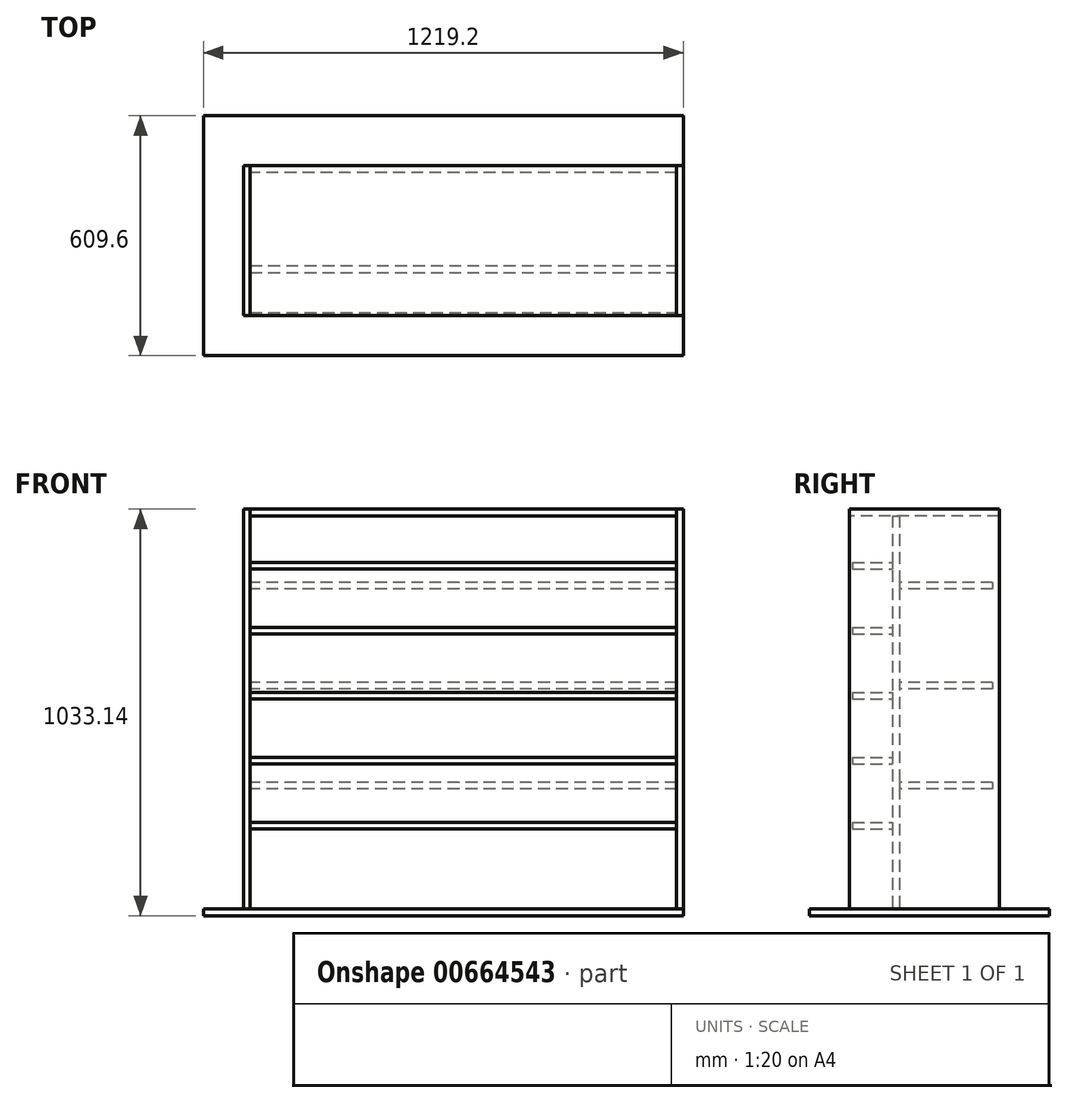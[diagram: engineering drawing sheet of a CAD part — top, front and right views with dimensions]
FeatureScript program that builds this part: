
annotation { "Feature Type Name" : "Feature", "Feature Type Description" : "" }
export const myFeature = defineFeature(function(context is Context, id is Id, definition is map)
    precondition{}
    {
        {
            var Q0;
            Q0=qCreatedBy(makeId("Top.planeOp"),FACE);
            var sketch = newSketch(context, id + "F0", { "sketchPlane" : qUnion([Q0])});
            skLineSegment(sketch, "E0.bottom", {"start": v(0, 0) * mm, "end": v(1219.2, 0) * mm});
            skLineSegment(sketch, "E0.top", {"start": v(0, 609.6) * mm, "end": v(1219.2, 609.6) * mm});
            skLineSegment(sketch, "E0.left", {"start": v(0, 0) * mm, "end": v(0, 609.6) * mm});
            skLineSegment(sketch, "E0.right", {"start": v(1219.2, 0) * mm, "end": v(1219.2, 609.6) * mm});
            skSolve(sketch);
        }
        {
            var Q0;
            Q0 = qSketchRegion(id + "F0", true);
            extrude(context, id + "F1", {"entities" : qUnion([Q0]), "depth" : 17.14 * mm, "offsetDistance" : 25.4 * mm});
        }
        {
            var Q0;
            Q0=makeQuery(id+"F1.opExtrude","CAP_FACE",FACE,{"disambiguationData":[OSD([sQuery(id+"F0.wireOp",EDGE,"E0.bottom"),sQuery(id+"F0.wireOp",EDGE,"E0.top"),sQuery(id+"F0.wireOp",EDGE,"E0.left"),sQuery(id+"F0.wireOp",EDGE,"E0.right")])],"isStart":false});
            var sketch = newSketch(context, id + "F2", { "sketchPlane" : qUnion([Q0])});
            skLineSegment(sketch, "E1.bottom", {"start": v(118.75, 101.6) * mm, "end": v(101.6, 101.6) * mm});
            skLineSegment(sketch, "E1.top", {"start": v(118.74, 482.6) * mm, "end": v(101.6, 482.6) * mm});
            skLineSegment(sketch, "E1.left", {"start": v(118.75, 101.6) * mm, "end": v(118.74, 482.6) * mm});
            skLineSegment(sketch, "E1.right", {"start": v(101.6, 101.6) * mm, "end": v(101.6, 482.6) * mm});
            skSolve(sketch);
        }
        {
            var Q0;
            Q0=makeQuery(id+"F2.imprint","IMPRINT",FACE,{"disambiguationData":[TD([[makeQuery(id+"F2.imprint","IMPRINT",EDGE,{"derivedFrom":sQuery(id+"F2.wireOp",EDGE,"E1.bottom")}),-1.0]])]});
            extrude(context, id + "F3", {"entities" : qUnion([Q0]), "depth" : 1016 * mm, "offsetDistance" : 25.4 * mm});
        }
        {
            var Q0;
            {var subQ0=sQuery(id+"F0.wireOp",EDGE,"E0.top");var subQ1=sQuery(id+"F0.wireOp",EDGE,"E0.right");var subQ2=sQuery(id+"F0.wireOp",EDGE,"E0.bottom");Q0=makeQuery(id+"F3.boolean.opBoolean","SPLIT",FACE,{"disambiguationData":[TD([makeQuery(id+"F1.opExtrude","SWEPT_FACE",FACE,{"disambiguationData":[OSD([subQ1])]})])],"derivedFrom":makeQuery(id+"F1.opExtrude","CAP_FACE",FACE,{"disambiguationData":[OSD([subQ2,subQ0,sQuery(id+"F0.wireOp",EDGE,"E0.left"),subQ1])],"isStart":false})});}
            var sketch = newSketch(context, id + "F4", { "sketchPlane" : qUnion([Q0])});
            skLineSegment(sketch, "E2.bottom", {"start": v(118.74, 211.45) * mm, "end": v(1202.06, 211.45) * mm});
            skLineSegment(sketch, "E2.top", {"start": v(118.74, 228.6) * mm, "end": v(1202.06, 228.6) * mm});
            skLineSegment(sketch, "E2.left", {"start": v(118.75, 211.45) * mm, "end": v(118.75, 228.6) * mm});
            skLineSegment(sketch, "E2.right", {"start": v(1202.06, 211.46) * mm, "end": v(1202.06, 228.6) * mm});
            skSolve(sketch);
        }
        {
            var Q0;
            Q0 = qSketchRegion(id + "F4", true);
            extrude(context, id + "F5", {"entities" : qUnion([Q0]), "depth" : 998.86 * mm, "offsetDistance" : 25.4 * mm});
        }
        {
            var Q0;
            {var subQ0=sQuery(id+"F0.wireOp",EDGE,"E0.top");var subQ1=sQuery(id+"F0.wireOp",EDGE,"E0.right");var subQ2=sQuery(id+"F0.wireOp",EDGE,"E0.bottom");Q0=makeQuery(id+"F3.boolean.opBoolean","SPLIT",FACE,{"disambiguationData":[TD([makeQuery(id+"F1.opExtrude","SWEPT_FACE",FACE,{"disambiguationData":[OSD([subQ1])]})])],"derivedFrom":makeQuery(id+"F1.opExtrude","CAP_FACE",FACE,{"disambiguationData":[OSD([subQ2,subQ0,sQuery(id+"F0.wireOp",EDGE,"E0.left"),subQ1])],"isStart":false})});}
            var sketch = newSketch(context, id + "F6", { "sketchPlane" : qUnion([Q0])});
            skLineSegment(sketch, "E3.bottom", {"start": v(1219.2, 101.6) * mm, "end": v(1202.06, 101.6) * mm});
            skLineSegment(sketch, "E3.top", {"start": v(1219.2, 482.6) * mm, "end": v(1202.06, 482.6) * mm});
            skLineSegment(sketch, "E3.left", {"start": v(1219.2, 101.6) * mm, "end": v(1219.2, 482.6) * mm});
            skLineSegment(sketch, "E3.right", {"start": v(1202.06, 101.6) * mm, "end": v(1202.06, 482.6) * mm});
            skSolve(sketch);
        }
        {
            var Q0;
            Q0 = qSketchRegion(id + "F6", true);
            extrude(context, id + "F7", {"entities" : qUnion([Q0]), "depth" : 1016 * mm, "offsetDistance" : 25.4 * mm});
        }
        {
            var Q0;
            Q0=makeQuery(id+"F5.opExtrude","SWEPT_FACE",FACE,{"disambiguationData":[OSD([sQuery(id+"F4.wireOp",EDGE,"E2.top")])]});
            var sketch = newSketch(context, id + "F8", { "sketchPlane" : qUnion([Q0])});
            skLineSegment(sketch, "E4.bottom", {"start": v(-1202.06, 321.95) * mm, "end": v(-118.75, 321.95) * mm});
            skLineSegment(sketch, "E4.top", {"start": v(-1202.06, 339.1) * mm, "end": v(-118.74, 339.1) * mm});
            skLineSegment(sketch, "E4.left", {"start": v(-1202.06, 321.95) * mm, "end": v(-1202.06, 339.1) * mm});
            skLineSegment(sketch, "E4.right", {"start": v(-118.75, 321.95) * mm, "end": v(-118.75, 339.1) * mm});
            skLineSegment(sketch, "E5.0.1.0", {"start": v(-1202.06, 593.1) * mm, "end": v(-118.74, 593.1) * mm});
            skLineSegment(sketch, "E5.0.1.1", {"start": v(-1202.06, 575.95) * mm, "end": v(-118.75, 575.95) * mm});
            skLineSegment(sketch, "E5.0.1.2", {"start": v(-1202.06, 575.95) * mm, "end": v(-1202.06, 593.1) * mm});
            skLineSegment(sketch, "E5.0.1.3", {"start": v(-118.75, 575.95) * mm, "end": v(-118.75, 593.1) * mm});
            skLineSegment(sketch, "E5.0.2.0", {"start": v(-1202.06, 847.1) * mm, "end": v(-118.74, 847.1) * mm});
            skLineSegment(sketch, "E5.0.2.1", {"start": v(-1202.06, 829.95) * mm, "end": v(-118.75, 829.95) * mm});
            skLineSegment(sketch, "E5.0.2.2", {"start": v(-1202.06, 829.95) * mm, "end": v(-1202.06, 847.1) * mm});
            skLineSegment(sketch, "E5.0.2.3", {"start": v(-118.75, 829.95) * mm, "end": v(-118.75, 847.1) * mm});
            skLineSegment(sketch, "E5.direction1", {"start": v(-1202.06, 321.95) * mm, "end": v(-1176.65, 321.95) * mm, "construction": true});
            skLineSegment(sketch, "E5.direction2", {"start": v(-1202.06, 321.95) * mm, "end": v(-1202.06, 575.95) * mm, "construction": true});
            skSolve(sketch);
        }
        {
            var Q0;
            Q0 = qSketchRegion(id + "F8", true);
            extrude(context, id + "F9", {"entities" : qUnion([Q0]), "depth" : 236.85 * mm, "offsetDistance" : 25.4 * mm});
        }
        {
            var Q0;
            Q0=makeQuery(id+"F5.opExtrude","SWEPT_FACE",FACE,{"disambiguationData":[OSD([sQuery(id+"F4.wireOp",EDGE,"E2.bottom")])]});
            var sketch = newSketch(context, id + "F10", { "sketchPlane" : qUnion([Q0])});
            skLineSegment(sketch, "E6.bottom", {"start": v(118.74, 220.35) * mm, "end": v(1202.06, 220.35) * mm});
            skLineSegment(sketch, "E6.top", {"start": v(118.74, 237.5) * mm, "end": v(1202.06, 237.5) * mm});
            skLineSegment(sketch, "E6.left", {"start": v(118.75, 220.35) * mm, "end": v(118.75, 237.5) * mm});
            skLineSegment(sketch, "E6.right", {"start": v(1202.06, 220.35) * mm, "end": v(1202.06, 237.5) * mm});
            skLineSegment(sketch, "E7.0.1.0", {"start": v(118.74, 402.6) * mm, "end": v(1202.06, 402.6) * mm});
            skLineSegment(sketch, "E7.0.1.1", {"start": v(118.74, 385.45) * mm, "end": v(1202.06, 385.45) * mm});
            skLineSegment(sketch, "E7.0.1.2", {"start": v(1202.06, 385.45) * mm, "end": v(1202.06, 402.6) * mm});
            skLineSegment(sketch, "E7.0.1.3", {"start": v(118.75, 385.45) * mm, "end": v(118.75, 402.6) * mm});
            skLineSegment(sketch, "E7.0.2.0", {"start": v(118.74, 567.7) * mm, "end": v(1202.06, 567.7) * mm});
            skLineSegment(sketch, "E7.0.2.1", {"start": v(118.74, 550.55) * mm, "end": v(1202.06, 550.55) * mm});
            skLineSegment(sketch, "E7.0.2.2", {"start": v(1202.06, 550.55) * mm, "end": v(1202.06, 567.7) * mm});
            skLineSegment(sketch, "E7.0.2.3", {"start": v(118.75, 550.55) * mm, "end": v(118.75, 567.7) * mm});
            skLineSegment(sketch, "E7.0.3.0", {"start": v(118.74, 732.8) * mm, "end": v(1202.06, 732.8) * mm});
            skLineSegment(sketch, "E7.0.3.1", {"start": v(118.74, 715.65) * mm, "end": v(1202.06, 715.65) * mm});
            skLineSegment(sketch, "E7.0.3.2", {"start": v(1202.06, 715.65) * mm, "end": v(1202.06, 732.8) * mm});
            skLineSegment(sketch, "E7.0.3.3", {"start": v(118.75, 715.65) * mm, "end": v(118.75, 732.8) * mm});
            skLineSegment(sketch, "E7.0.4.0", {"start": v(118.74, 897.9) * mm, "end": v(1202.06, 897.9) * mm});
            skLineSegment(sketch, "E7.0.4.1", {"start": v(118.74, 880.75) * mm, "end": v(1202.06, 880.75) * mm});
            skLineSegment(sketch, "E7.0.4.2", {"start": v(1202.06, 880.75) * mm, "end": v(1202.06, 897.9) * mm});
            skLineSegment(sketch, "E7.0.4.3", {"start": v(118.75, 880.75) * mm, "end": v(118.75, 897.9) * mm});
            skLineSegment(sketch, "E7.direction1", {"start": v(118.74, 220.35) * mm, "end": v(144.14, 220.35) * mm, "construction": true});
            skLineSegment(sketch, "E7.direction2", {"start": v(118.74, 220.35) * mm, "end": v(118.74, 385.45) * mm, "construction": true});
            skSolve(sketch);
        }
        {
            var Q0;
            Q0=makeQuery(id+"F10.imprint","IMPRINT",FACE,{"disambiguationData":[TD([[makeQuery(id+"F10.imprint","IMPRINT",EDGE,{"derivedFrom":sQuery(id+"F10.wireOp",EDGE,"E7.0.4.0")}),-1.0]])]});
            var Q1;
            Q1=makeQuery(id+"F10.imprint","IMPRINT",FACE,{"disambiguationData":[TD([[makeQuery(id+"F10.imprint","IMPRINT",EDGE,{"derivedFrom":sQuery(id+"F10.wireOp",EDGE,"E7.0.3.0")}),-1.0]])]});
            var Q2;
            Q2=makeQuery(id+"F10.imprint","IMPRINT",FACE,{"disambiguationData":[TD([[makeQuery(id+"F10.imprint","IMPRINT",EDGE,{"derivedFrom":sQuery(id+"F10.wireOp",EDGE,"E7.0.2.0")}),-1.0]])]});
            var Q3;
            Q3=makeQuery(id+"F10.imprint","IMPRINT",FACE,{"disambiguationData":[TD([[makeQuery(id+"F10.imprint","IMPRINT",EDGE,{"derivedFrom":sQuery(id+"F10.wireOp",EDGE,"E7.0.1.0")}),-1.0]])]});
            var Q4;
            Q4=makeQuery(id+"F10.imprint","IMPRINT",FACE,{"disambiguationData":[TD([[makeQuery(id+"F10.imprint","IMPRINT",EDGE,{"derivedFrom":sQuery(id+"F10.wireOp",EDGE,"E6.bottom")}),1.0]])]});
            extrude(context, id + "F11", {"entities" : qUnion([Q0, Q1, Q2, Q3, Q4]), "depth" : 101.6 * mm, "offsetDistance" : 25.4 * mm});
        }
        {
            var Q0;
            Q0=makeQuery(id+"F3.opExtrude","SWEPT_FACE",FACE,{"disambiguationData":[OSD([sQuery(id+"F2.wireOp",EDGE,"E1.left")])]});
            var sketch = newSketch(context, id + "F12", { "sketchPlane" : qUnion([Q0])});
            skLineSegment(sketch, "E8.bottom", {"start": v(101.6, 1033.14) * mm, "end": v(482.6, 1033.14) * mm});
            skLineSegment(sketch, "E8.top", {"start": v(101.6, 1016) * mm, "end": v(482.6, 1016) * mm});
            skLineSegment(sketch, "E8.left", {"start": v(101.6, 1033.14) * mm, "end": v(101.6, 1016) * mm});
            skLineSegment(sketch, "E8.right", {"start": v(482.6, 1033.14) * mm, "end": v(482.6, 1016) * mm});
            skSolve(sketch);
        }
        {
            var Q0;
            Q0 = qSketchRegion(id + "F12", true);
            extrude(context, id + "F13", {"entities" : qUnion([Q0]), "endBound" : BoundingType.UP_TO_NEXT, "depth" : 25.4 * mm, "offsetDistance" : 25.4 * mm});
        }
    });
